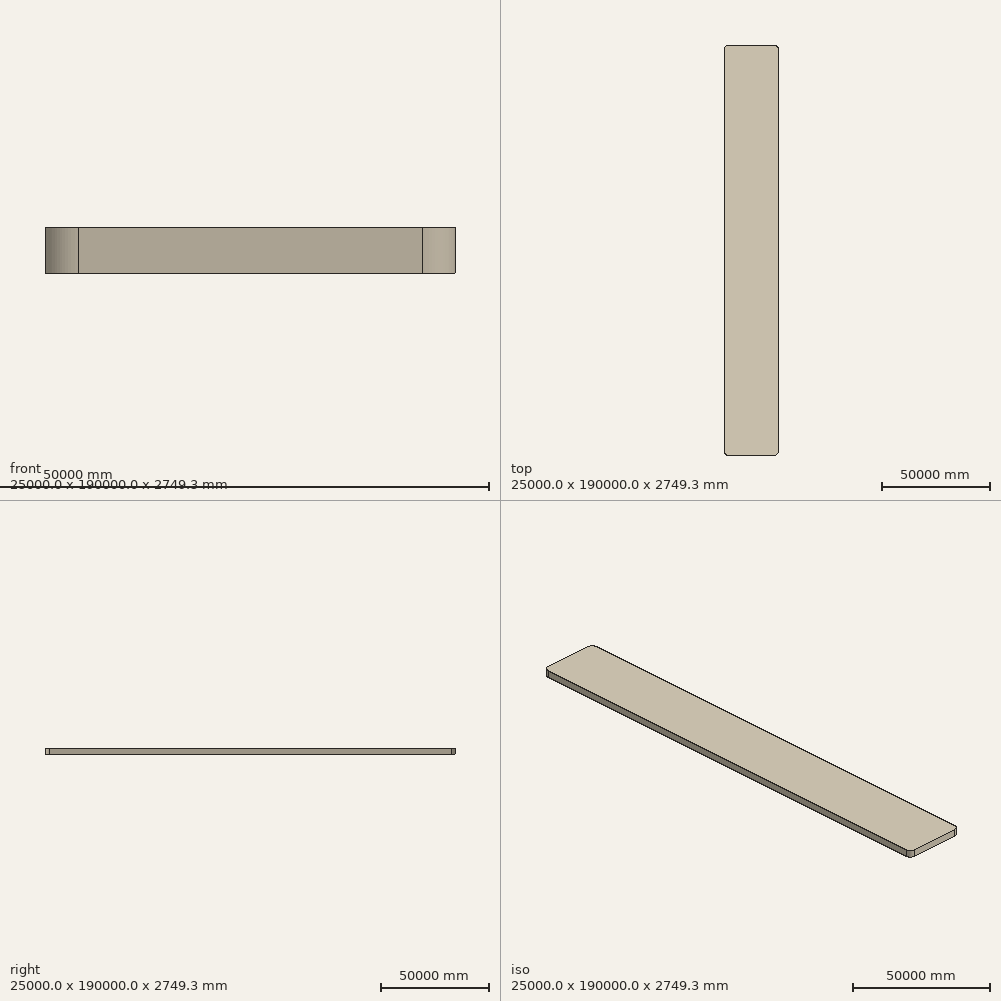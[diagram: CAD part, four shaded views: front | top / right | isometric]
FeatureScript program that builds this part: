
annotation { "Feature Type Name" : "Feature", "Feature Type Description" : "" }
export const myFeature = defineFeature(function(context is Context, id is Id, definition is map)
    precondition{}
    {
        {
            var Q0;
            Q0=qCreatedBy(makeId("Top.planeOp"),FACE);
            var sketch = newSketch(context, id + "F0", { "sketchPlane" : qUnion([Q0])});
            skLineSegment(sketch, "E0.bottom", {"start": v(-11865, 95000) * mm, "end": v(11865, 95000) * mm});
            skLineSegment(sketch, "E0.top", {"start": v(-11865, -95000) * mm, "end": v(11865, -95000) * mm});
            skLineSegment(sketch, "E0.left", {"start": v(-12500, 94365) * mm, "end": v(-12500, -94365) * mm});
            skLineSegment(sketch, "E0.right", {"start": v(12500, 94365) * mm, "end": v(12500, -94365) * mm});
            skPoint(sketch, "E0.middle", {"position": v(0, 0) * mm});
            skPoint(sketch, "E1.visualSharp", {"position": v(-12500, 95000) * mm});
            skPoint(sketch, "E2.visualSharp", {"position": v(12500, 95000) * mm});
            skPoint(sketch, "E3.visualSharp", {"position": v(-12500, -95000) * mm});
            skPoint(sketch, "E4.visualSharp", {"position": v(12500, -95000) * mm});
            skLineSegment(sketch, "E5", {"start": v(11865, -95000) * mm, "end": v(12500, -95000) * mm});
            skLineSegment(sketch, "E6", {"start": v(12500, -94365) * mm, "end": v(12500, -95000) * mm});
            skLineSegment(sketch, "E7", {"start": v(-12500, -95000) * mm, "end": v(-12500, -94365) * mm});
            skLineSegment(sketch, "E8", {"start": v(-12500, -95000) * mm, "end": v(-11865, -95000) * mm});
            skLineSegment(sketch, "E9", {"start": v(-12500, 95000) * mm, "end": v(-12500, 94365) * mm});
            skLineSegment(sketch, "E10", {"start": v(-12500, 95000) * mm, "end": v(-11865, 95000) * mm});
            skLineSegment(sketch, "E11", {"start": v(11865, 95000) * mm, "end": v(12500, 95000) * mm});
            skLineSegment(sketch, "E12", {"start": v(12500, 94365) * mm, "end": v(12500, 95000) * mm});
            skSolve(sketch);
        }
        {
            var Q0;
            Q0=makeQuery(id+"F0.imprint","IMPRINT",FACE,{"disambiguationData":[TD([[makeQuery(id+"F0.imprint","IMPRINT",EDGE,{"derivedFrom":sQuery(id+"F0.wireOp",EDGE,"E0.bottom")}),-1.0]])]});
            extrude(context, id + "F1", {"entities" : qUnion([Q0]), "depth" : 2749.3 * mm});
        }
        {
            var Q0;
            Q0=makeQuery(id+"F1.opExtrude","SWEPT_EDGE",EDGE,{"disambiguationData":[OSD([sQuery(id+"F0.wireOp",EDGE,"E7"),sQuery(id+"F0.wireOp",EDGE,"E8")])]});
            var Q1;
            Q1=makeQuery(id+"F1.opExtrude","SWEPT_EDGE",EDGE,{"disambiguationData":[OSD([sQuery(id+"F0.wireOp",EDGE,"E5"),sQuery(id+"F0.wireOp",EDGE,"E6")])]});
            var Q2;
            Q2=makeQuery(id+"F1.opExtrude","SWEPT_EDGE",EDGE,{"disambiguationData":[OSD([sQuery(id+"F0.wireOp",EDGE,"E9"),sQuery(id+"F0.wireOp",EDGE,"E10")])]});
            var Q3;
            Q3=makeQuery(id+"F1.opExtrude","SWEPT_EDGE",EDGE,{"disambiguationData":[OSD([sQuery(id+"F0.wireOp",EDGE,"E11"),sQuery(id+"F0.wireOp",EDGE,"E12")])]});
            fillet(context, id + "F2", {"entities" : qUnion([Q0, Q1, Q2, Q3]), "radius" : 2000 * mm, "tangentPropagation" : true, "allowEdgeOverflow" : false});
        }
    });
